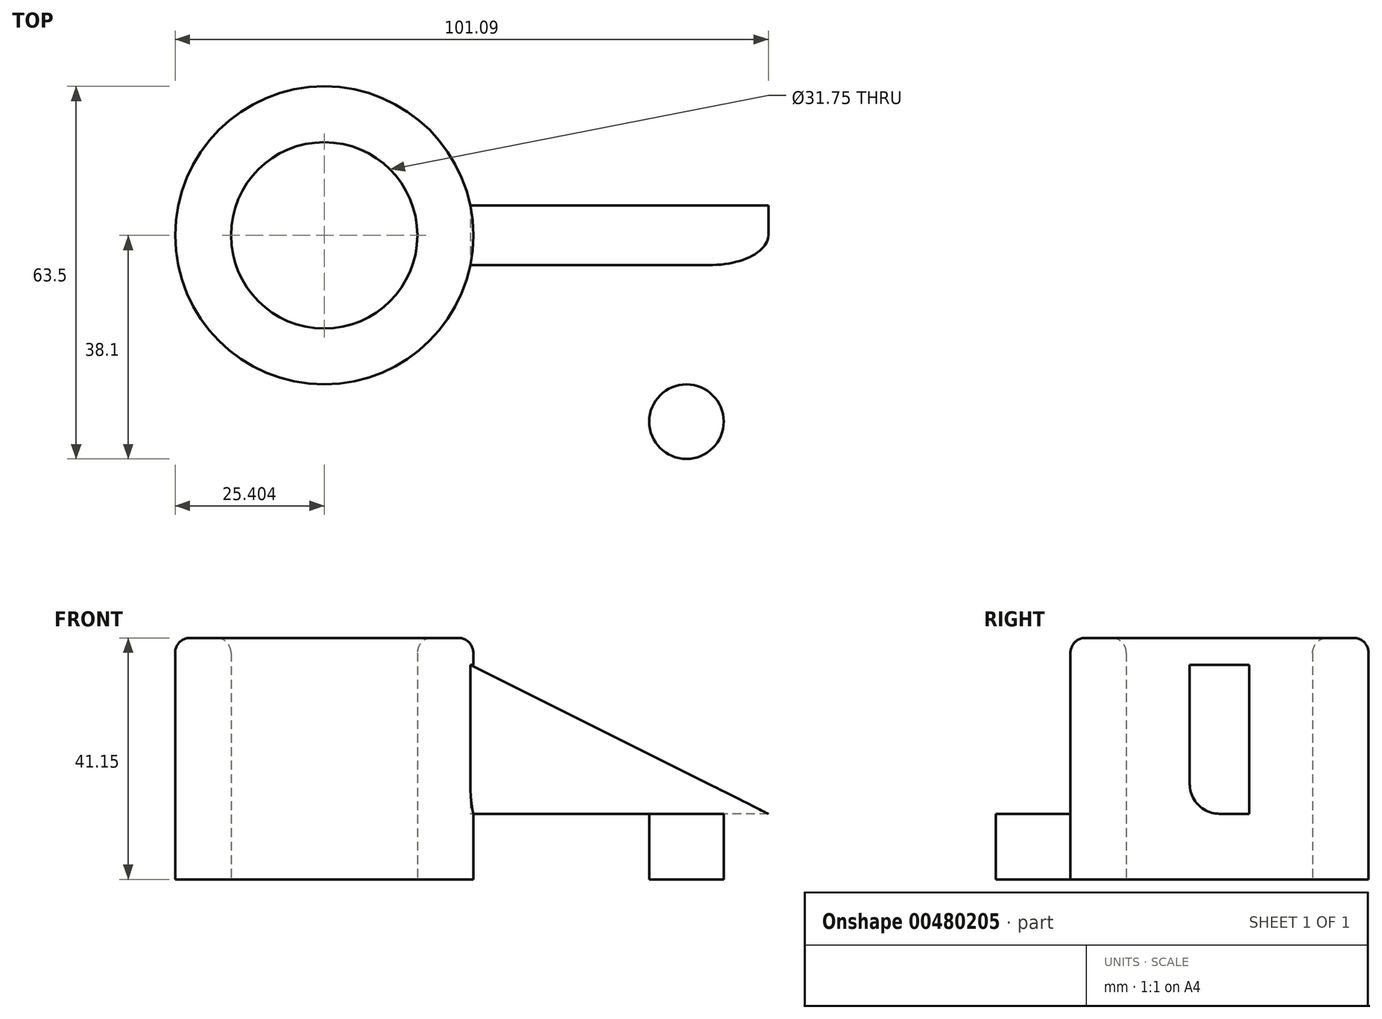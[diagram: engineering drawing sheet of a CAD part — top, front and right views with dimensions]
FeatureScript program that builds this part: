
annotation { "Feature Type Name" : "Feature", "Feature Type Description" : "" }
export const myFeature = defineFeature(function(context is Context, id is Id, definition is map)
    precondition{}
    {
        {
            var Q0;
            Q0=qCreatedBy(makeId("Top.planeOp"),FACE);
            var sketch = newSketch(context, id + "F0", { "sketchPlane" : qUnion([Q0])});
            skCircle(sketch, "E0", {"center": v(-46.56, 0) * mm, "radius": 25.4 * mm});
            skLineSegment(sketch, "E1", {"start": v(-47.02, 25.4) * mm, "end": v(34.03, 59.16) * mm});
            skLineSegment(sketch, "E2", {"start": v(34.03, 59.16) * mm, "end": v(34.03, -57.54) * mm});
            skLineSegment(sketch, "E3", {"start": v(34.03, -57.54) * mm, "end": v(-47.3, -25.39) * mm});
            skCircle(sketch, "E4", {"center": v(-46.56, 0) * mm, "radius": 15.88 * mm});
            skSolve(sketch);
        }
        {
            var Q0;
            Q0=makeQuery(id+"F0.imprint","IMPRINT",FACE,{"disambiguationData":[TD([[makeQuery(id+"F0.imprint","IMPRINT",EDGE,{"derivedFrom":sQuery(id+"F0.wireOp",EDGE,"E4")}),-1.0]])]});
            extrude(context, id + "F1", {"entities" : qUnion([Q0]), "depth" : 41.15 * mm});
        }
        {
            var Q0;
            {var subQ0=sQuery(id+"F0.wireOp",EDGE,"E1");Q0=makeQuery(id+"F0.imprint","IMPRINT",FACE,{"disambiguationData":[TD([[makeQuery(id+"F0.imprint","IMPRINT",EDGE,{"derivedFrom":subQ0}),-1.0]])]});}
            extrude(context, id + "F2", {"entities" : qUnion([Q0]), "operationType" : NewBodyOperationType.ADD, "depth" : 11.18 * mm});
        }
        {
            var Q0;
            Q0=makeQuery(id+"F2.opExtrude","CAP_FACE",FACE,{"disambiguationData":[OSD([sQuery(id+"F0.wireOp",EDGE,"E0"),sQuery(id+"F0.wireOp",EDGE,"E1"),sQuery(id+"F0.wireOp",EDGE,"E2"),sQuery(id+"F0.wireOp",EDGE,"E3")])],"isStart":false});
            var sketch = newSketch(context, id + "F3", { "sketchPlane" : qUnion([Q0])});
            skCircle(sketch, "E5", {"center": v(15.18, 31.75) * mm, "radius": 6.35 * mm});
            skCircle(sketch, "E6.MirrorC", {"center": v(15.18, -31.75) * mm, "radius": 6.35 * mm});
            skSolve(sketch);
        }
        {
            var Q0;
            Q0=makeQuery(id+"F3.imprint","IMPRINT",FACE,{"disambiguationData":[TD([[makeQuery(id+"F3.imprint","IMPRINT",EDGE,{"derivedFrom":sQuery(id+"F3.wireOp",EDGE,"E5")}),1.0]])]});
            extrude(context, id + "F4", {"entities" : qUnion([Q0]), "operationType" : NewBodyOperationType.REMOVE, "endBound" : BoundingType.THROUGH_ALL, "oppositeDirection" : true, "depth" : 15.77 * mm});
        }
        {
            var Q0;
            Q0=makeQuery(id+"F3.imprint","IMPRINT",FACE,{"disambiguationData":[TD([[makeQuery(id+"F3.imprint","IMPRINT",EDGE,{"derivedFrom":sQuery(id+"F3.wireOp",EDGE,"E6.MirrorC")}),-1.0]])]});
            extrude(context, id + "F5", {"entities" : qUnion([Q0]), "operationType" : NewBodyOperationType.REMOVE, "oppositeDirection" : true, "depth" : 15.77 * mm});
        }
        {
            var Q0;
            Q0=makeQuery(id+"F3.imprint","IMPRINT",FACE,{"disambiguationData":[TD([[makeQuery(id+"F3.imprint","IMPRINT",EDGE,{"derivedFrom":sQuery(id+"F3.wireOp",EDGE,"E5")}),-1.0]])]});
            var sketch = newSketch(context, id + "F6", { "sketchPlane" : qUnion([Q0])});
            skLineSegment(sketch, "E7", {"start": v(30.73, -4.13) * mm, "end": v(30.73, 10.2) * mm, "construction": true});
            skSolve(sketch);
        }
        {
            var Q0;
            Q0=makeQuery(id+"F6.imprint","IMPRINT",FACE,{"disambiguationData":[TD([[makeQuery(id+"F6.imprint","IMPRINT",EDGE,{"derivedFrom":makeQuery(id+"F3.imprint","IMPRINT",EDGE,{"derivedFrom":sQuery(id+"F3.wireOp",EDGE,"E5")})}),-1.0]])]});
            var sketch = newSketch(context, id + "F7", { "sketchPlane" : qUnion([Q0])});
            skLineSegment(sketch, "E8", {"start": v(29.13, -5.08) * mm, "end": v(-21.67, -5.08) * mm});
            skLineSegment(sketch, "E9", {"start": v(29.13, 5.08) * mm, "end": v(-21.67, 5.08) * mm});
            skLineSegment(sketch, "E10", {"start": v(29.13, -5.08) * mm, "end": v(29.13, 5.08) * mm});
            skSolve(sketch);
        }
        {
            var Q0;
            {var subQ0=sQuery(id+"F7.wireOp",EDGE,"E8");Q0=makeQuery(id+"F7.imprint","IMPRINT",FACE,{"disambiguationData":[TD([[makeQuery(id+"F7.imprint","IMPRINT",EDGE,{"derivedFrom":subQ0}),-1.0]])]});}
            extrude(context, id + "F8", {"entities" : qUnion([Q0]), "operationType" : NewBodyOperationType.ADD, "depth" : 25.4 * mm});
        }
        {
            var Q0;
            Q0=makeQuery(id+"F8.opExtrude","SWEPT_FACE",FACE,{"disambiguationData":[OSD([sQuery(id+"F7.wireOp",EDGE,"E8")])]});
            var sketch = newSketch(context, id + "F9", { "sketchPlane" : qUnion([Q0])});
            skLineSegment(sketch, "E11", {"start": v(-21.67, 36.58) * mm, "end": v(29.13, 11.18) * mm});
            skSolve(sketch);
        }
        {
            var Q0;
            Q0=makeQuery(id+"F9.imprint","IMPRINT",FACE,{"disambiguationData":[TD([[makeQuery(id+"F9.imprint","IMPRINT",EDGE,{"derivedFrom":sQuery(id+"F9.wireOp",EDGE,"E11")}),1.0]])]});
            extrude(context, id + "F10", {"entities" : qUnion([Q0]), "operationType" : NewBodyOperationType.REMOVE, "oppositeDirection" : true, "depth" : 25.4 * mm});
        }
        {
            var Q0;
            Q0=makeQuery(id+"F8.opExtrude","SWEPT_EDGE",EDGE,{"disambiguationData":[OSD([sQuery(id+"F0.wireOp",EDGE,"E0"),sQuery(id+"F7.wireOp",EDGE,"E8")])]});
            var Q1;
            Q1=makeQuery(id+"F8.opExtrude","CAP_EDGE",EDGE,{"disambiguationData":[OSD([sQuery(id+"F7.wireOp",EDGE,"E8")])],"isStart":true});
            var Q2;
            {var subQ0=sQuery(id+"F0.wireOp",EDGE,"E0");var subQ1=sQuery(id+"F0.wireOp",EDGE,"E3");Q2=makeQuery(id+"F8.boolean.opBoolean","SPLIT",EDGE,{"disambiguationData":[TD([makeQuery(id+"F2.opExtrude","SWEPT_FACE",FACE,{"disambiguationData":[OSD([subQ1])]})])],"derivedFrom":makeQuery(id+"F2.opExtrude","CAP_EDGE",EDGE,{"disambiguationData":[OSD([subQ0])],"isStart":false})});}
            fillet(context, id + "F11", {"entities" : qUnion([Q0, Q1, Q2]), "radius" : 5.08 * mm, "tangentPropagation" : true, "allowEdgeOverflow" : false});
        }
        {
            var Q0;
            Q0=makeQuery(id+"F1.opExtrude","CAP_EDGE",EDGE,{"disambiguationData":[OSD([sQuery(id+"F0.wireOp",EDGE,"E0")])],"isStart":false});
            var Q1;
            Q1=makeQuery(id+"F1.opExtrude","CAP_EDGE",EDGE,{"disambiguationData":[OSD([sQuery(id+"F0.wireOp",EDGE,"E4")])],"isStart":false});
            fillet(context, id + "F12", {"entities" : qUnion([Q0, Q1]), "radius" : 2.54 * mm, "tangentPropagation" : true, "allowEdgeOverflow" : false});
        }
    });
